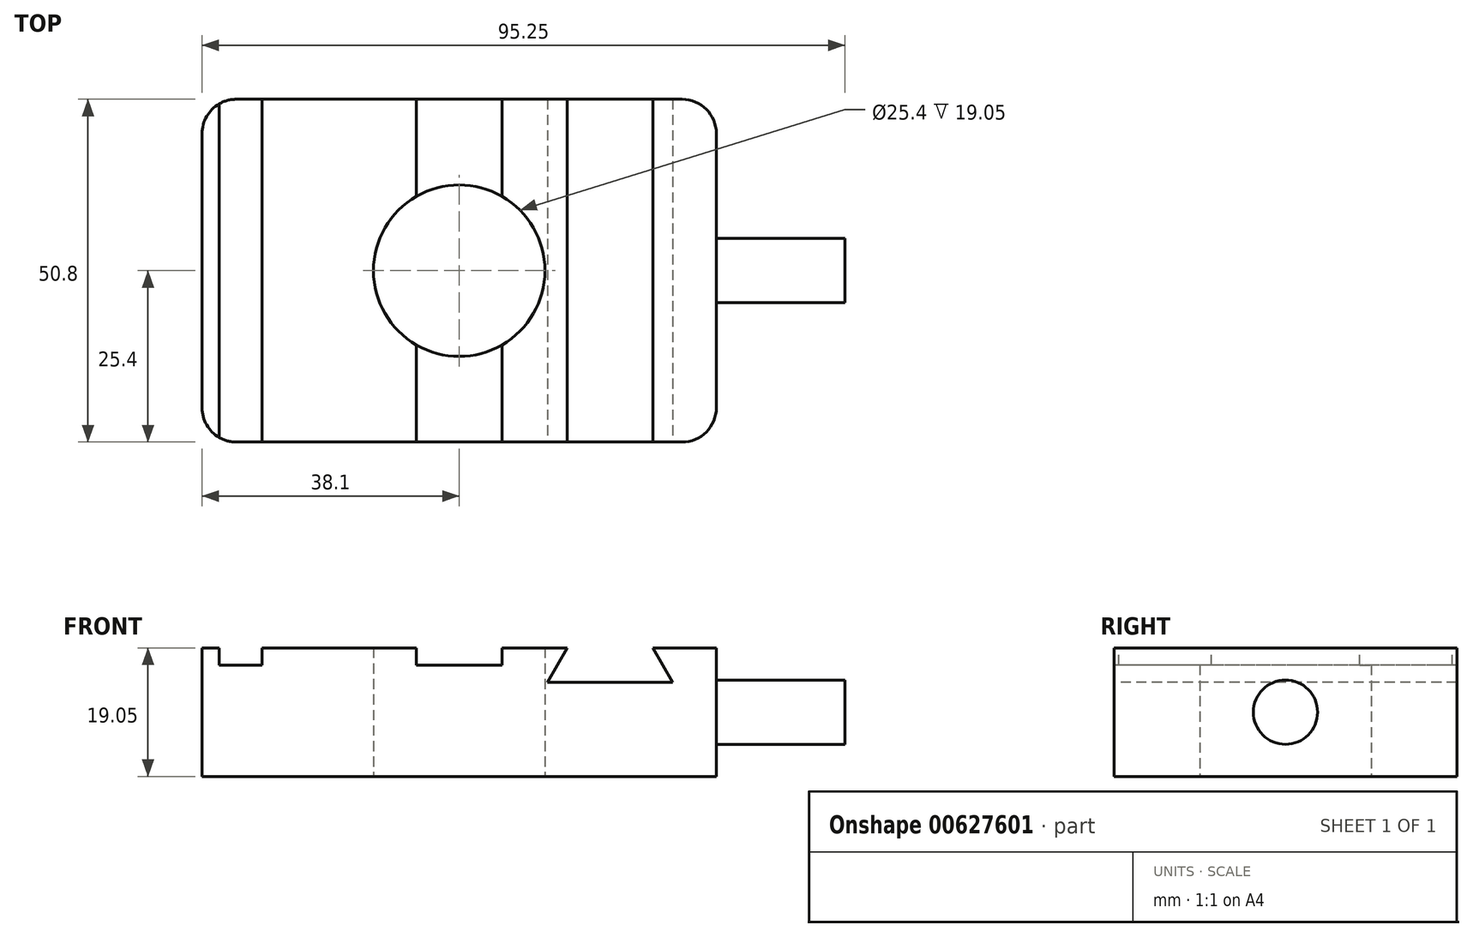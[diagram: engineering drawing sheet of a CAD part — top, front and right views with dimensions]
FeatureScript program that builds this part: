
annotation { "Feature Type Name" : "Feature", "Feature Type Description" : "" }
export const myFeature = defineFeature(function(context is Context, id is Id, definition is map)
    precondition{}
    {
        {
            var Q0;
            Q0=qCreatedBy(makeId("Top.planeOp"),FACE);
            var sketch = newSketch(context, id + "F0", { "sketchPlane" : qUnion([Q0])});
            skLineSegment(sketch, "E0.bottom", {"start": v(-38.1, 25.4) * mm, "end": v(38.1, 25.4) * mm});
            skLineSegment(sketch, "E0.top", {"start": v(-38.1, -25.4) * mm, "end": v(38.1, -25.4) * mm});
            skLineSegment(sketch, "E0.left", {"start": v(-38.1, 25.4) * mm, "end": v(-38.1, -25.4) * mm});
            skLineSegment(sketch, "E0.right", {"start": v(38.1, 25.4) * mm, "end": v(38.1, -25.4) * mm});
            skPoint(sketch, "E0.middle", {"position": v(0, 0) * mm});
            skCircle(sketch, "E1", {"center": v(0, 0) * mm, "radius": 12.7 * mm});
            skSolve(sketch);
        }
        {
            var Q0;
            Q0=makeQuery(id+"F0.imprint","IMPRINT",FACE,{"disambiguationData":[TD([[makeQuery(id+"F0.imprint","IMPRINT",EDGE,{"derivedFrom":sQuery(id+"F0.wireOp",EDGE,"E0.bottom")}),-1.0]])]});
            extrude(context, id + "F1", {"entities" : qUnion([Q0]), "depth" : 19.05 * mm, "offsetDistance" : 25.4 * mm});
        }
        {
            var Q0;
            Q0=makeQuery(id+"F1.opExtrude","SWEPT_EDGE",EDGE,{"disambiguationData":[OSD([sQuery(id+"F0.wireOp",EDGE,"E0.top"),sQuery(id+"F0.wireOp",EDGE,"E0.left")])]});
            fillet(context, id + "F2", {"entities" : qUnion([Q0]), "radius" : 5.08 * mm, "tangentPropagation" : true, "allowEdgeOverflow" : false});
        }
        {
            var Q0;
            Q0=makeQuery(id+"F1.opExtrude","SWEPT_EDGE",EDGE,{"disambiguationData":[OSD([sQuery(id+"F0.wireOp",EDGE,"E0.top"),sQuery(id+"F0.wireOp",EDGE,"E0.right")])]});
            var Q1;
            Q1=makeQuery(id+"F1.opExtrude","SWEPT_EDGE",EDGE,{"disambiguationData":[OSD([sQuery(id+"F0.wireOp",EDGE,"E0.bottom"),sQuery(id+"F0.wireOp",EDGE,"E0.right")])]});
            fillet(context, id + "F3", {"entities" : qUnion([Q0, Q1]), "radius" : 5.08 * mm, "tangentPropagation" : true, "allowEdgeOverflow" : false});
        }
        {
            var Q0;
            Q0=makeQuery(id+"F1.opExtrude","SWEPT_EDGE",EDGE,{"disambiguationData":[OSD([sQuery(id+"F0.wireOp",EDGE,"E0.bottom"),sQuery(id+"F0.wireOp",EDGE,"E0.left")])]});
            fillet(context, id + "F4", {"entities" : qUnion([Q0]), "radius" : 5.08 * mm, "tangentPropagation" : true, "allowEdgeOverflow" : false});
        }
        {
            var Q0;
            Q0=makeQuery(id+"F1.opExtrude","CAP_FACE",FACE,{"disambiguationData":[OSD([sQuery(id+"F0.wireOp",EDGE,"E0.bottom"),sQuery(id+"F0.wireOp",EDGE,"E0.top"),sQuery(id+"F0.wireOp",EDGE,"E0.left"),sQuery(id+"F0.wireOp",EDGE,"E0.right"),sQuery(id+"F0.wireOp",EDGE,"E1")])],"isStart":false});
            var sketch = newSketch(context, id + "F5", { "sketchPlane" : qUnion([Q0])});
            skLineSegment(sketch, "E2.bottom", {"start": v(-35.56, 25.4) * mm, "end": v(-29.2, 25.4) * mm});
            skLineSegment(sketch, "E2.top", {"start": v(-35.56, -25.4) * mm, "end": v(-29.2, -25.4) * mm});
            skLineSegment(sketch, "E2.left", {"start": v(-35.56, 25.4) * mm, "end": v(-35.56, -25.4) * mm});
            skLineSegment(sketch, "E2.right", {"start": v(-29.2, 25.4) * mm, "end": v(-29.2, -25.4) * mm});
            skPoint(sketch, "E3", {"position": v(0, 0) * mm});
            skLineSegment(sketch, "E4", {"start": v(-6.35, 25.4) * mm, "end": v(-6.35, -25.4) * mm});
            skLineSegment(sketch, "E5", {"start": v(6.35, -25.4) * mm, "end": v(6.35, 25.4) * mm});
            skLineSegment(sketch, "E6", {"start": v(6.35, 25.4) * mm, "end": v(-6.35, 25.4) * mm});
            skLineSegment(sketch, "E7", {"start": v(0, 25.4) * mm, "end": v(0, -25.4) * mm, "construction": true});
            skSolve(sketch);
        }
        {
            var Q0;
            {var subQ0=sQuery(id+"F5.wireOp",EDGE,"E2.right");Q0=makeQuery(id+"F5.imprint","IMPRINT",FACE,{"disambiguationData":[TD([[makeQuery(id+"F5.imprint","IMPRINT",EDGE,{"derivedFrom":subQ0}),-1.0]])]});}
            var Q1;
            {var subQ0=sQuery(id+"F5.wireOp",EDGE,"E4");var subQ1=makeQuery(id+"F1.opExtrude","CAP_EDGE",EDGE,{"disambiguationData":[OSD([sQuery(id+"F0.wireOp",EDGE,"E0.top")])],"isStart":false});var subQ2=makeQuery(id+"F5.imprint","INTERSECT",VERTEX,{"derivedFrom":[subQ1,subQ0]});Q1=makeQuery(id+"F5.imprint","IMPRINT",FACE,{"disambiguationData":[TD([[makeQuery(id+"F5.imprint","IMPRINT",EDGE,{"disambiguationData":[TD([[subQ2,1.0]])],"derivedFrom":subQ0}),1.0]])]});}
            var Q2;
            {var subQ0=sQuery(id+"F5.wireOp",EDGE,"E6");Q2=makeQuery(id+"F5.imprint","IMPRINT",FACE,{"disambiguationData":[TD([[makeQuery(id+"F5.imprint","IMPRINT",EDGE,{"derivedFrom":subQ0}),-1.0]])]});}
            extrude(context, id + "F6", {"entities" : qUnion([Q0, Q1, Q2]), "operationType" : NewBodyOperationType.REMOVE, "oppositeDirection" : true, "depth" : 2.54 * mm, "offsetDistance" : 25.4 * mm});
        }
        {
            var Q0;
            Q0=makeQuery(id+"F1.opExtrude","SWEPT_FACE",FACE,{"disambiguationData":[OSD([sQuery(id+"F0.wireOp",EDGE,"E0.right")])]});
            var sketch = newSketch(context, id + "F7", { "sketchPlane" : qUnion([Q0])});
            skCircle(sketch, "E8", {"center": v(0, 9.53) * mm, "radius": 4.76 * mm});
            skPoint(sketch, "E8.centerSnap0", {"position": v(-20.32, 9.53) * mm});
            skSolve(sketch);
        }
        {
            var Q0;
            Q0=makeQuery(id+"F7.imprint","IMPRINT",FACE,{"disambiguationData":[TD([[makeQuery(id+"F7.imprint","IMPRINT",EDGE,{"derivedFrom":sQuery(id+"F7.wireOp",EDGE,"E8")}),1.0]])]});
            extrude(context, id + "F8", {"entities" : qUnion([Q0]), "operationType" : NewBodyOperationType.ADD, "depth" : 19.05 * mm, "offsetDistance" : 25.4 * mm});
        }
        {
            var Q0;
            Q0=makeQuery(id+"F1.opExtrude","SWEPT_FACE",FACE,{"disambiguationData":[OSD([sQuery(id+"F0.wireOp",EDGE,"E0.top")])]});
            var sketch = newSketch(context, id + "F9", { "sketchPlane" : qUnion([Q0])});
            skLineSegment(sketch, "E9", {"start": v(16, 19.05) * mm, "end": v(13.07, 13.97) * mm});
            skLineSegment(sketch, "E10", {"start": v(31.63, 13.97) * mm, "end": v(13.07, 13.97) * mm});
            skLineSegment(sketch, "E11", {"start": v(31.63, 13.97) * mm, "end": v(28.7, 19.05) * mm});
            skLineSegment(sketch, "E12", {"start": v(28.7, 19.05) * mm, "end": v(16, 19.05) * mm});
            skLineSegment(sketch, "E13", {"start": v(22.35, 13.97) * mm, "end": v(22.35, 19.05) * mm, "construction": true});
            skSolve(sketch);
        }
        {
            var Q0;
            Q0=makeQuery(id+"F9.imprint","IMPRINT",FACE,{"disambiguationData":[TD([[makeQuery(id+"F9.imprint","IMPRINT",EDGE,{"derivedFrom":sQuery(id+"F9.wireOp",EDGE,"E9")}),1.0]])]});
            extrude(context, id + "F10", {"entities" : qUnion([Q0]), "operationType" : NewBodyOperationType.REMOVE, "endBound" : BoundingType.THROUGH_ALL, "oppositeDirection" : true, "depth" : 25.4 * mm, "offsetDistance" : 25.4 * mm});
        }
    });
